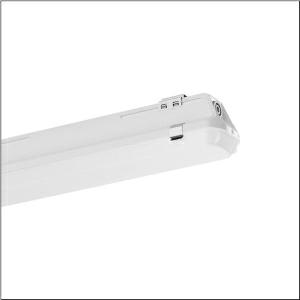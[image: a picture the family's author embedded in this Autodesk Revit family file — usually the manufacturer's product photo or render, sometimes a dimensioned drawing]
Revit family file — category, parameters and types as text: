
# Revit family: monsun_r__11_51fp208p430h_cbd4
name_source: partatom
category: Lighting Fixtures
units: mm (PartAtom-declared; Revit-internal decimal feet)

## family parameters
Cut with Voids When Loaded = No
Host = Face
Light Source = No
Part Type = Normal
Room Calculation Point = No
Round Connector Dimension = Use Diameter
Shared = No

## types (1)
- Monsun® 11 (1 x LED, 3990 lm, 24.8 W, 4000K)
    Apparent Load = 25 VA
    CIE Flux Codes = 45 75 93 94 100
    Color Rendering = 80
    Color Temperature = 4000K
    Default Elevation = 1800 mm
    Description = Monsun® 11, damp-proof luminaire, chain hanger, primary optical cover: enclosure, of PC, light emission: direct distribution, primary light characteristic: symmetric, installation type: suspended mounting, surface-mounted, horizontal mounting, vertical mounting, LED, rated luminous flux: 3.990lm, luminous efficacy: 161lm/W, light colour: 840, colour temperature: 4000K, control gear: ECG, with terminal, 3-pole, max. 2.5mm², mains connection: 220..240V, AC, 50/60Hz, rated input power: 25W, luminaire housing, of glass-fibre reinforced polyester, uncoated, bright grey, incl. chain hanger, length: 1.590mm, width: 90mm, height: 88mm, clip for enclosure, of stainless steel (V2A), ceiling mounting element, of stainless steel (V2A), chain hanger, of stainless steel (V2A), protection rating (complete): IP66, insulation class (complete): insulation class I (protective earthing), certification: CE, ENEC, VDE, UKCA, protection symbol: D, impact resistance: IK08, permissible operating ambient temperature: -35..+40°C, standard: EN 50419, EN 60598-2-1, no direct snow, no direct sun, no direct rain, for indoor or canopied outdoor use, corresponds to IFS (International Featured Standards) requirements for safety and quality in the food industry, contact your sales advisor before using the luminaires in applications with unclear chemical exposure, large temperature fluctuations or condensation-forming humidity, LABS conformity tested according to VDMA 24364:2018-05, packaging unit: 1 piece
    Height = 89 mm
    Lamp = 1 x LED
    Lamp Light Flux = 3990 lm
    Lamp Power = 24.8 W
    Lamp count = 1
    Length = 1590 mm
    Luminous efficacy = 161 lm/W
    Manufacturer = Siteco
    ModVariant = No
    Model = 51FP208P430H
    Mounting Place = Ceiling
    Mounting Type = Surface mounted
    Number of Poles = 1
    OnlyDefault = Yes
    Power Factor = 1
    Product Name = Monsun® 11
    Product group = damp-proof luminaire
    ProductGroupID = 300
    Protection Class = Protection class I
    Protection Degree = IP 66
    RLX_Detail_Level = 1
    RLX_Emergency_Light_Flux = 0 lm
    RLX_Emergency_Type = 0
    RLX_Emergency_Type_DB = No
    RlxData = <blob elided: 88577 chars, md5=f49faad4>
    Socket = socket
    Standby Power = 0 W
    System Light Flux = 3990 lm
    System Power = 25 W
    Type Comments = Product without accessories
    Type Image = l_1004748.jpg
    URL = http://relux.com
    VarID = ---
    Voltage = 0 V
    Weight = 0.00 kg
    Width = 90 mm

## geometry (parser evidence)
native form markers: Blend x4, Sweep x15
no freeform markers — native parametric forms only
